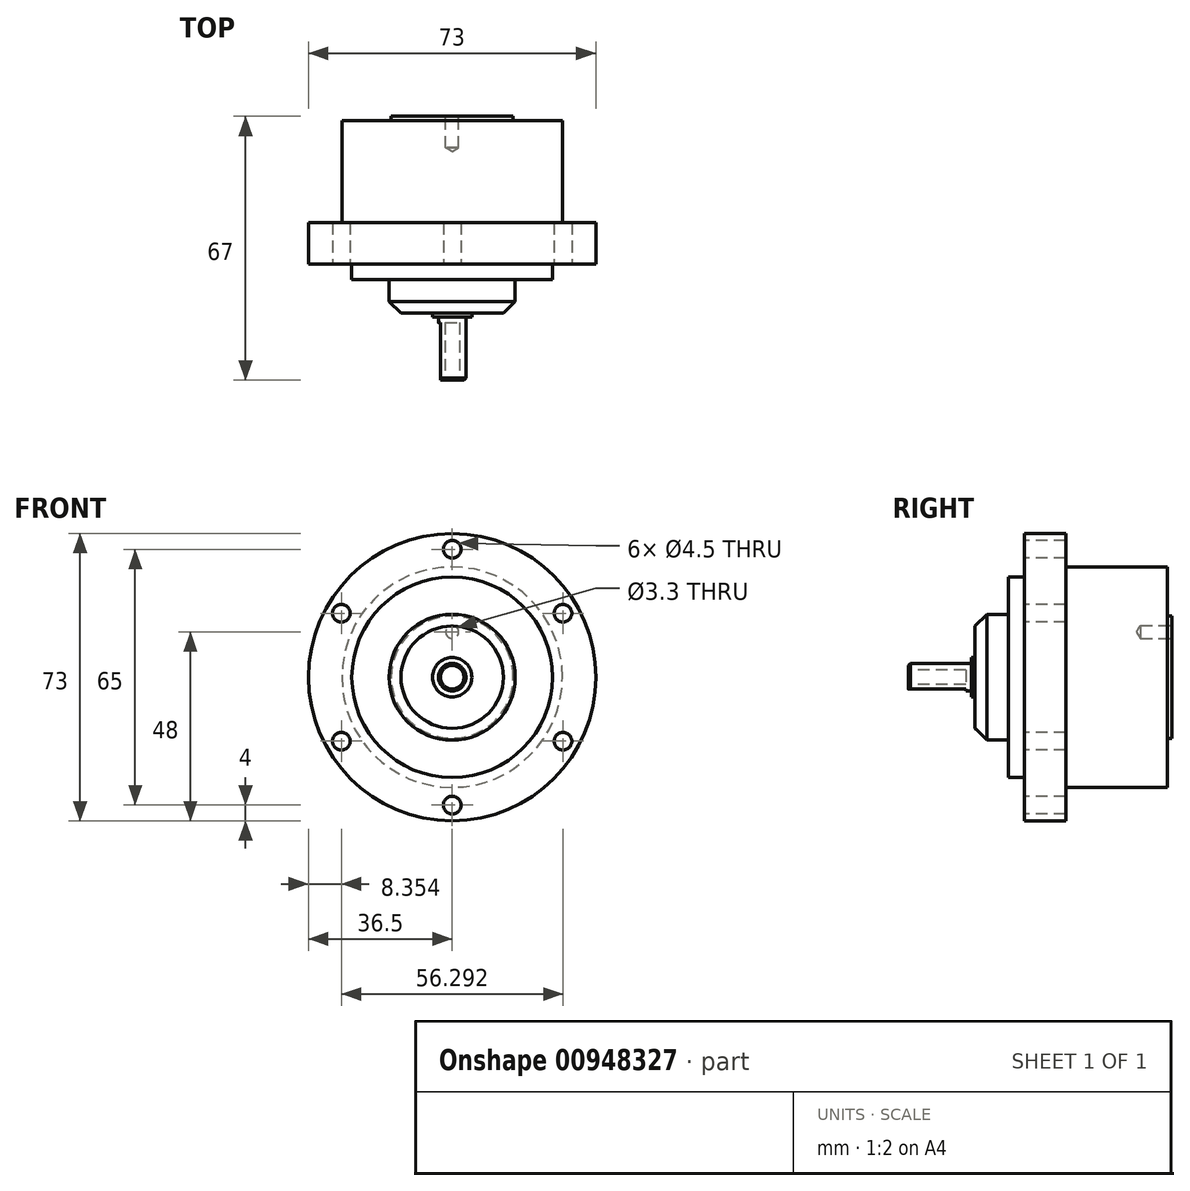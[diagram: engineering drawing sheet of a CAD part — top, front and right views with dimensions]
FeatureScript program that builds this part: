
annotation { "Feature Type Name" : "Feature", "Feature Type Description" : "" }
export const myFeature = defineFeature(function(context is Context, id is Id, definition is map)
    precondition{}
    {
        {
            var Q0;
            Q0=qCreatedBy(makeId("Front.planeOp"),FACE);
            var sketch = newSketch(context, id + "F0", { "sketchPlane" : qUnion([Q0])});
            skCircle(sketch, "E0", {"center": v(0, 0) * mm, "radius": 36.5 * mm});
            skSolve(sketch);
        }
        {
            var Q0;
            Q0=makeQuery(id+"F0.imprint","IMPRINT",FACE,{"disambiguationData":[TD([[makeQuery(id+"F0.imprint","IMPRINT",EDGE,{"derivedFrom":sQuery(id+"F0.wireOp",EDGE,"E0")}),1.0]])]});
            extrude(context, id + "F1", {"entities" : qUnion([Q0]), "oppositeDirection" : true, "depth" : 10.5 * mm, "offsetDistance" : 25.4 * mm});
        }
        {
            var Q0;
            Q0=makeQuery(id+"F1.opExtrude","CAP_FACE",FACE,{"disambiguationData":[OSD([sQuery(id+"F0.wireOp",EDGE,"E0")])],"isStart":true});
            var sketch = newSketch(context, id + "F2", { "sketchPlane" : qUnion([Q0])});
            skCircle(sketch, "E1", {"center": v(0, 0) * mm, "radius": 25.5 * mm});
            skSolve(sketch);
        }
        {
            var Q0;
            Q0=makeQuery(id+"F2.imprint","IMPRINT",FACE,{"disambiguationData":[TD([[makeQuery(id+"F2.imprint","IMPRINT",EDGE,{"derivedFrom":sQuery(id+"F2.wireOp",EDGE,"E1")}),1.0]])]});
            extrude(context, id + "F3", {"entities" : qUnion([Q0]), "operationType" : NewBodyOperationType.ADD, "depth" : 4 * mm, "offsetDistance" : 25.4 * mm});
        }
        {
            var Q0;
            Q0=makeQuery(id+"F3.opExtrude","CAP_FACE",FACE,{"disambiguationData":[OSD([sQuery(id+"F2.wireOp",EDGE,"E1")])],"isStart":false});
            var sketch = newSketch(context, id + "F4", { "sketchPlane" : qUnion([Q0])});
            skCircle(sketch, "E2", {"center": v(0, 0) * mm, "radius": 16 * mm});
            skSolve(sketch);
        }
        {
            var Q0;
            Q0=makeQuery(id+"F4.imprint","IMPRINT",FACE,{"disambiguationData":[TD([[makeQuery(id+"F4.imprint","IMPRINT",EDGE,{"derivedFrom":sQuery(id+"F4.wireOp",EDGE,"E2")}),1.0]])]});
            extrude(context, id + "F5", {"entities" : qUnion([Q0]), "operationType" : NewBodyOperationType.ADD, "depth" : 8.5 * mm, "offsetDistance" : 25.4 * mm});
        }
        {
            var Q0;
            Q0=makeQuery(id+"F5.opExtrude","CAP_FACE",FACE,{"disambiguationData":[OSD([sQuery(id+"F4.wireOp",EDGE,"E2")])],"isStart":false});
            var sketch = newSketch(context, id + "F6", { "sketchPlane" : qUnion([Q0])});
            skCircle(sketch, "E3", {"center": v(0, 0) * mm, "radius": 5 * mm});
            skSolve(sketch);
        }
        {
            var Q0;
            Q0=makeQuery(id+"F6.imprint","IMPRINT",FACE,{"disambiguationData":[TD([[makeQuery(id+"F6.imprint","IMPRINT",EDGE,{"derivedFrom":sQuery(id+"F6.wireOp",EDGE,"E3")}),1.0]])]});
            extrude(context, id + "F7", {"entities" : qUnion([Q0]), "operationType" : NewBodyOperationType.ADD, "depth" : 1 * mm, "offsetDistance" : 25.4 * mm});
        }
        {
            var Q0;
            Q0=makeQuery(id+"F7.opExtrude","CAP_FACE",FACE,{"disambiguationData":[OSD([sQuery(id+"F6.wireOp",EDGE,"E3")])],"isStart":false});
            var sketch = newSketch(context, id + "F8", { "sketchPlane" : qUnion([Q0])});
            skCircle(sketch, "E4", {"center": v(0, 0) * mm, "radius": 3.5 * mm});
            skSolve(sketch);
        }
        {
            var Q0;
            Q0=makeQuery(id+"F8.imprint","IMPRINT",FACE,{"disambiguationData":[TD([[makeQuery(id+"F8.imprint","IMPRINT",EDGE,{"derivedFrom":sQuery(id+"F8.wireOp",EDGE,"E4")}),1.0]])]});
            extrude(context, id + "F9", {"entities" : qUnion([Q0]), "operationType" : NewBodyOperationType.ADD, "depth" : 16 * mm, "offsetDistance" : 25.4 * mm});
        }
        {
            var Q0;
            Q0=makeQuery(id+"F9.opExtrude","CAP_FACE",FACE,{"disambiguationData":[OSD([sQuery(id+"F8.wireOp",EDGE,"E4")])],"isStart":false});
            var sketch = newSketch(context, id + "F10", { "sketchPlane" : qUnion([Q0])});
            skLineSegment(sketch, "E5", {"start": v(-3, 1.8) * mm, "end": v(-3, -1.8) * mm});
            skLineSegment(sketch, "E6", {"start": v(-1.8, -3) * mm, "end": v(1.8, -3) * mm});
            skPoint(sketch, "E7", {"position": v(0, 3.5) * mm});
            skPoint(sketch, "E8", {"position": v(3.5, 0) * mm});
            skArc(sketch, "E9.0", {"start": v(-3, 1.8) * mm, "mid": v(-3.5, 0) * mm, "end": v(-3, -1.8) * mm});
            skArc(sketch, "E10.trimOffspring", {"start": v(-1.8, -3) * mm, "mid": v(0, -3.5) * mm, "end": v(1.8, -3) * mm});
            skSolve(sketch);
        }
        {
            var Q0;
            Q0=makeQuery(id+"F10.imprint","IMPRINT",FACE,{"disambiguationData":[TD([[makeQuery(id+"F10.imprint","IMPRINT",EDGE,{"derivedFrom":sQuery(id+"F10.wireOp",EDGE,"E6")}),-1.0]])]});
            var Q1;
            Q1=makeQuery(id+"F10.imprint","IMPRINT",FACE,{"disambiguationData":[TD([[makeQuery(id+"F10.imprint","IMPRINT",EDGE,{"derivedFrom":sQuery(id+"F10.wireOp",EDGE,"E5")}),-1.0]])]});
            extrude(context, id + "F11", {"entities" : qUnion([Q0, Q1]), "operationType" : NewBodyOperationType.REMOVE, "oppositeDirection" : true, "depth" : 14.6 * mm, "offsetDistance" : 25.4 * mm});
        }
        {
            var Q0;
            Q0=makeQuery(id+"F11.boolean.opBoolean","COPY",EDGE,{"derivedFrom":makeQuery(id+"F11.opExtrude","CAP_EDGE",EDGE,{"disambiguationData":[OSD([sQuery(id+"F10.wireOp",EDGE,"E6")])],"isStart":true})});
            var Q1;
            Q1=makeQuery(id+"F11.boolean.opBoolean","SPLIT",EDGE,{"disambiguationData":[OD(0.0)],"derivedFrom":makeQuery(id+"F9.opExtrude","CAP_EDGE",EDGE,{"disambiguationData":[OSD([sQuery(id+"F8.wireOp",EDGE,"E4")])],"isStart":false})});
            var Q2;
            Q2=makeQuery(id+"F11.boolean.opBoolean","COPY",EDGE,{"derivedFrom":makeQuery(id+"F11.opExtrude","CAP_EDGE",EDGE,{"disambiguationData":[OSD([sQuery(id+"F10.wireOp",EDGE,"E5")])],"isStart":true})});
            var Q3;
            Q3=makeQuery(id+"F11.boolean.opBoolean","SPLIT",EDGE,{"disambiguationData":[OD(1.0)],"derivedFrom":makeQuery(id+"F9.opExtrude","CAP_EDGE",EDGE,{"disambiguationData":[OSD([sQuery(id+"F8.wireOp",EDGE,"E4")])],"isStart":false})});
            chamfer(context, id + "F12", {"entities" : qUnion([Q0, Q1, Q2, Q3]), "width" : .5 * mm, "tangentPropagation" : true});
        }
        {
            var Q0;
            Q0=makeQuery(id+"F5.opExtrude","CAP_EDGE",EDGE,{"disambiguationData":[OSD([sQuery(id+"F4.wireOp",EDGE,"E2")])],"isStart":false});
            chamfer(context, id + "F13", {"entities" : qUnion([Q0]), "width" : 3 * mm, "tangentPropagation" : true});
        }
        {
            var Q0;
            Q0=makeQuery(id+"F1.opExtrude","CAP_FACE",FACE,{"disambiguationData":[OSD([sQuery(id+"F0.wireOp",EDGE,"E0")])],"isStart":true});
            var sketch = newSketch(context, id + "F14", { "sketchPlane" : qUnion([Q0])});
            skCircle(sketch, "E11", {"center": v(0, 0) * mm, "radius": 32.5 * mm, "construction": true});
            skCircle(sketch, "E12", {"center": v(0, 32.5) * mm, "radius": 2.25 * mm});
            skCircle(sketch, "E13.1.0", {"center": v(-28.15, 16.25) * mm, "radius": 2.25 * mm});
            skCircle(sketch, "E13.2.0", {"center": v(-28.15, -16.25) * mm, "radius": 2.25 * mm});
            skCircle(sketch, "E14.1.3.0", {"center": v(0, -32.5) * mm, "radius": 2.25 * mm});
            skCircle(sketch, "E14.1.4.0", {"center": v(28.15, -16.25) * mm, "radius": 2.25 * mm});
            skCircle(sketch, "E14.1.5.0", {"center": v(28.15, 16.25) * mm, "radius": 2.25 * mm});
            skSolve(sketch);
        }
        {
            var Q0;
            Q0 = qSketchRegion(id + "F14", true);
            extrude(context, id + "F15", {"entities" : qUnion([Q0]), "operationType" : NewBodyOperationType.REMOVE, "endBound" : BoundingType.UP_TO_NEXT, "oppositeDirection" : true, "depth" : 25.4 * mm, "offsetDistance" : 25.4 * mm});
        }
        {
            var Q0;
            Q0=makeQuery(id+"F1.opExtrude","CAP_FACE",FACE,{"disambiguationData":[OSD([sQuery(id+"F0.wireOp",EDGE,"E0")])],"isStart":false});
            var sketch = newSketch(context, id + "F16", { "sketchPlane" : qUnion([Q0])});
            skCircle(sketch, "E15", {"center": v(0, 0) * mm, "radius": 28 * mm});
            skSolve(sketch);
        }
        {
            var Q0;
            Q0=makeQuery(id+"F16.imprint","IMPRINT",FACE,{"disambiguationData":[TD([[makeQuery(id+"F16.imprint","IMPRINT",EDGE,{"derivedFrom":sQuery(id+"F16.wireOp",EDGE,"E15")}),1.0]])]});
            extrude(context, id + "F17", {"entities" : qUnion([Q0]), "operationType" : NewBodyOperationType.ADD, "depth" : 25.9 * mm, "offsetDistance" : 25.4 * mm});
        }
        {
            var Q0;
            Q0=makeQuery(id+"F17.opExtrude","CAP_FACE",FACE,{"disambiguationData":[OSD([sQuery(id+"F16.wireOp",EDGE,"E15")])],"isStart":false});
            var sketch = newSketch(context, id + "F18", { "sketchPlane" : qUnion([Q0])});
            skCircle(sketch, "E16", {"center": v(0, 0) * mm, "radius": 15.5 * mm});
            skSolve(sketch);
        }
        {
            var Q0;
            Q0=makeQuery(id+"F18.imprint","IMPRINT",FACE,{"disambiguationData":[TD([[makeQuery(id+"F18.imprint","IMPRINT",EDGE,{"derivedFrom":sQuery(id+"F18.wireOp",EDGE,"E16")}),1.0]])]});
            extrude(context, id + "F19", {"entities" : qUnion([Q0]), "operationType" : NewBodyOperationType.ADD, "depth" : 1.1 * mm, "offsetDistance" : 25.4 * mm});
        }
        {
            var Q0;
            Q0=makeQuery(id+"F19.opExtrude","CAP_FACE",FACE,{"disambiguationData":[OSD([sQuery(id+"F18.wireOp",EDGE,"E16")])],"isStart":false});
            var sketch = newSketch(context, id + "F20", { "sketchPlane" : qUnion([Q0])});
            skCircle(sketch, "E17", {"center": v(0, 0) * mm, "radius": 11.5 * mm, "construction": true});
            skPoint(sketch, "E18", {"position": v(0, 11.5) * mm});
            skSolve(sketch);
        }
        {
            var Q0;
            Q0=sQuery(id+"F20.wireOp",VERTEX,"E18");
            var Q1;
            Q1=makeQuery(id+"F1.opExtrude","SWEPT_BODY",BODY,{"disambiguationData":[OSD([sQuery(id+"F0.wireOp",EDGE,"E0")])]});
            hole(context, id + "F21", {"style" : HoleStyle.SIMPLE, "endStyle" : HoleEndStyle.BLIND, "standardTappedOrClearance" : lookupTablePath({ "standard" : "ISO", "engagement" : "75%", "pitch" : "0.7 mm", "size" : "M4", "type" : "Tapped" }), "standardBlindInLast" : lookupTablePath({ "standard" : "ISO", "fit" : "Normal", "engagement" : "75%", "pitch" : "0.7 mm", "size" : "M4", "type" : "Clearance & tapped" }), "holeDiameter" : 3.3 * mm, "majorDiameter" : 4 * mm, "showTappedDepth" : true, "holeDepth" : 8 * mm, "tappedDepth" : 5.9 * mm, "tapClearance" : 3, "locations" : qUnion([Q0]), "scope" : qUnion([Q1])});
        }
    });
